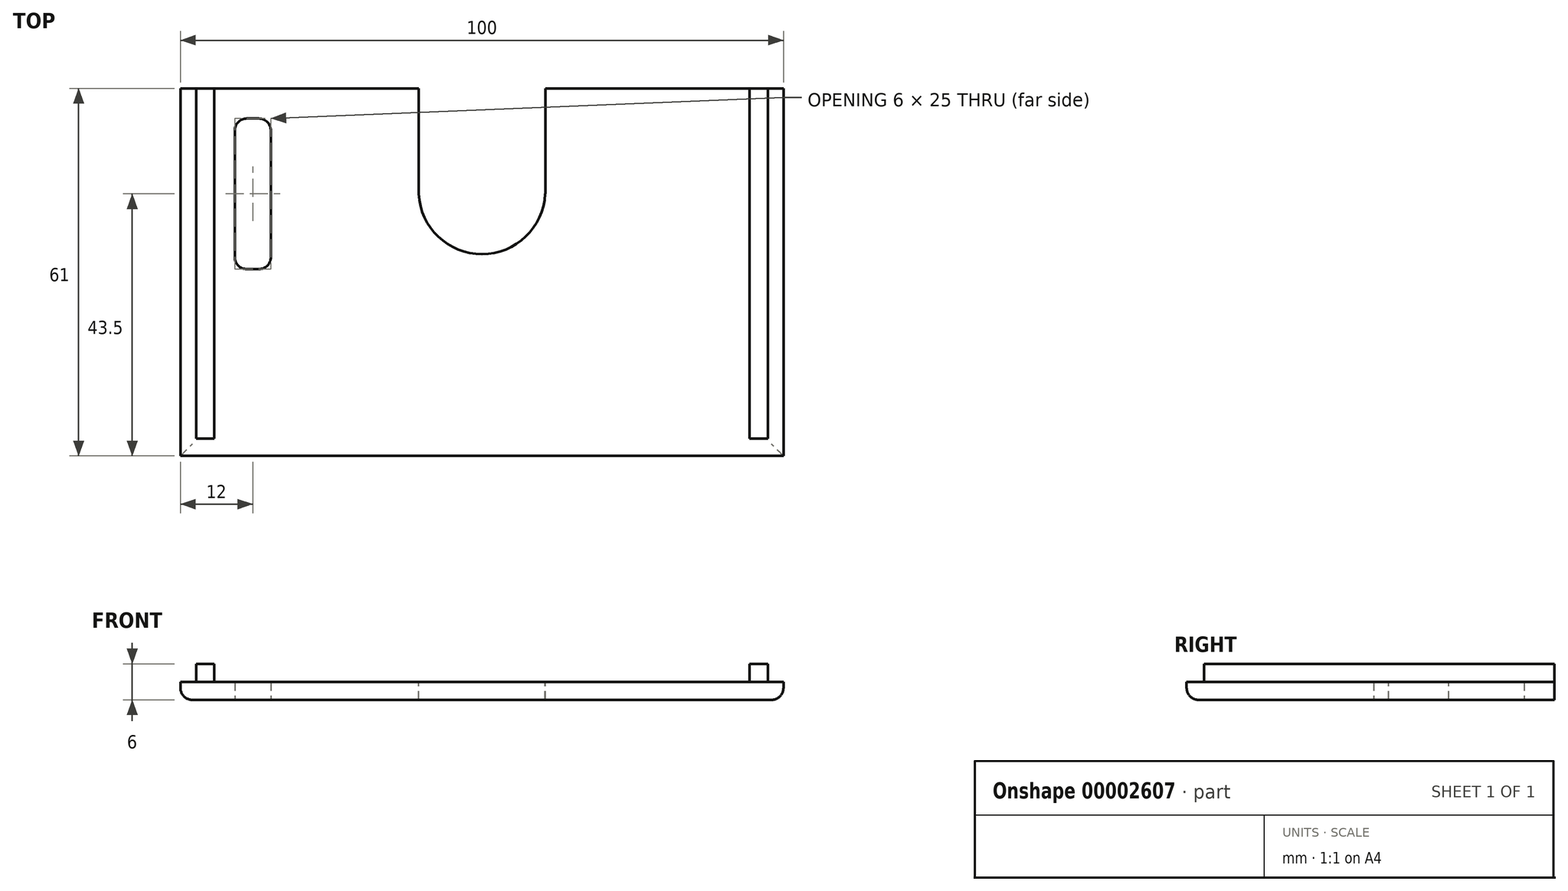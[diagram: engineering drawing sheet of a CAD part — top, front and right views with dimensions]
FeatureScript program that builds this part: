
annotation { "Feature Type Name" : "Feature", "Feature Type Description" : "" }
export const myFeature = defineFeature(function(context is Context, id is Id, definition is map)
    precondition{}
    {
        {
            var Q0;
            Q0=qCreatedBy(makeId("Top.planeOp"),FACE);
            var sketch = newSketch(context, id + "F0", { "sketchPlane" : qUnion([Q0])});
            skLineSegment(sketch, "E0.rect.bottom", {"start": v(-50, 30.5) * mm, "end": v(50, 30.5) * mm});
            skLineSegment(sketch, "E0.rect.top", {"start": v(-50, -30.5) * mm, "end": v(50, -30.5) * mm});
            skLineSegment(sketch, "E0.rect.left", {"start": v(-50, 30.5) * mm, "end": v(-50, -30.5) * mm});
            skLineSegment(sketch, "E0.rect.right", {"start": v(50, 30.5) * mm, "end": v(50, -30.5) * mm});
            skPoint(sketch, "E0.rect.middle", {"position": v(0, 0) * mm});
            skSolve(sketch);
        }
        {
            var Q0;
            Q0=makeQuery(id+"F0.imprint","IMPRINT",FACE,{"disambiguationData":[TD([[makeQuery(id+"F0.imprint","IMPRINT",EDGE,{"derivedFrom":sQuery(id+"F0.wireOp",EDGE,"E0.rect.bottom")}),-1.0]])]});
            extrude(context, id + "F1", {"entities" : qUnion([Q0]), "depth" : 3 * mm});
        }
        {
            var Q0;
            Q0=makeQuery(id+"F1.opExtrude","CAP_FACE",FACE,{"disambiguationData":[OSD([sQuery(id+"F0.wireOp",EDGE,"E0.rect.bottom"),sQuery(id+"F0.wireOp",EDGE,"E0.rect.top"),sQuery(id+"F0.wireOp",EDGE,"E0.rect.left"),sQuery(id+"F0.wireOp",EDGE,"E0.rect.right")])],"isStart":false});
            var sketch = newSketch(context, id + "F2", { "sketchPlane" : qUnion([Q0])});
            skLineSegment(sketch, "E1", {"start": v(0, 30.5) * mm, "end": v(0, 13.5) * mm, "construction": true});
            skCircle(sketch, "E2", {"center": v(0, 13.5) * mm, "radius": 10.5 * mm});
            skLineSegment(sketch, "E3", {"start": v(0, 30.5) * mm, "end": v(0, 22) * mm, "construction": true});
            skLineSegment(sketch, "E4.rect.bottom", {"start": v(-10.5, 31) * mm, "end": v(10.5, 31) * mm});
            skLineSegment(sketch, "E4.rect.top", {"start": v(-10.5, 13) * mm, "end": v(10.5, 13) * mm});
            skLineSegment(sketch, "E4.rect.left", {"start": v(-10.5, 31) * mm, "end": v(-10.5, 13) * mm});
            skLineSegment(sketch, "E4.rect.right", {"start": v(10.5, 31) * mm, "end": v(10.5, 13) * mm});
            skPoint(sketch, "E4.rect.middle", {"position": v(0, 22) * mm});
            skSolve(sketch);
        }
        {
            var Q0;
            {var subQ0=sQuery(id+"F2.wireOp",EDGE,"E4.rect.left");var subQ1=sQuery(id+"F2.wireOp",EDGE,"E2");var subQ2=makeQuery(id+"F2.imprint","INTERSECT",VERTEX,{"derivedFrom":[subQ1,subQ0]});var subQ3=sQuery(id+"F2.wireOp",EDGE,"E4.rect.top");var subQ5=makeQuery(id+"F2.imprint","INTERSECT",VERTEX,{"disambiguationData":[OD(0.0)],"derivedFrom":[subQ1,subQ3]});var subQ6=makeQuery(id+"F2.imprint","IMPRINT",EDGE,{"disambiguationData":[TD([[subQ2,-1.0]])],"derivedFrom":subQ1});var subQ9=sQuery(id+"F2.wireOp",EDGE,"E4.rect.right");var subQ10=makeQuery(id+"F2.imprint","INTERSECT",VERTEX,{"derivedFrom":[subQ1,subQ9]});var subQ12=makeQuery(id+"F2.imprint","IMPRINT",EDGE,{"disambiguationData":[TD([[subQ10,1.0]])],"derivedFrom":subQ1});var subQ13=makeQuery(id+"F2.imprint","IMPRINT",EDGE,{"disambiguationData":[TD([[subQ2,1.0]])],"derivedFrom":subQ1});var subQ18=sQuery(id+"F2.wireOp",EDGE,"E4.rect.bottom");Q0=qUnion([makeQuery(id+"F2.imprint","IMPRINT",FACE,{"disambiguationData":[TD([[subQ6,-1.0]])]}),makeQuery(id+"F2.imprint","IMPRINT",FACE,{"disambiguationData":[TD([[makeQuery(id+"F2.imprint","IMPRINT",EDGE,{"disambiguationData":[TD([[subQ5,-1.0]])],"derivedFrom":subQ1}),1.0]])]}),makeQuery(id+"F2.imprint","IMPRINT",FACE,{"disambiguationData":[TD([[subQ12,-1.0]])]}),makeQuery(id+"F2.imprint","IMPRINT",FACE,{"disambiguationData":[TD([[subQ13,1.0]])]}),makeQuery(id+"F2.imprint","IMPRINT",FACE,{"disambiguationData":[TD([[makeQuery(id+"F2.imprint","IMPRINT",EDGE,{"derivedFrom":subQ18}),-1.0]])]}),makeQuery(id+"F2.imprint","IMPRINT",FACE,{"disambiguationData":[TD([[subQ13,-1.0]])]})]);}
            extrude(context, id + "F3", {"entities" : qUnion([Q0]), "operationType" : NewBodyOperationType.REMOVE, "oppositeDirection" : true, "depth" : 25 * mm});
        }
        {
            var Q0;
            Q0=makeQuery(id+"F1.opExtrude","CAP_FACE",FACE,{"disambiguationData":[OSD([sQuery(id+"F0.wireOp",EDGE,"E0.rect.bottom"),sQuery(id+"F0.wireOp",EDGE,"E0.rect.top"),sQuery(id+"F0.wireOp",EDGE,"E0.rect.left"),sQuery(id+"F0.wireOp",EDGE,"E0.rect.right")])],"isStart":false});
            var sketch = newSketch(context, id + "F4", { "sketchPlane" : qUnion([Q0])});
            skLineSegment(sketch, "E5", {"start": v(-50, -30.5) * mm, "end": v(-44.4, -30.5) * mm, "construction": true});
            skLineSegment(sketch, "E6", {"start": v(-44.4, -30.5) * mm, "end": v(-44.4, -27.6) * mm, "construction": true});
            skLineSegment(sketch, "E7", {"start": v(-50, 30.5) * mm, "end": v(-47.4, 30.5) * mm, "construction": true});
            skLineSegment(sketch, "E8.bottom", {"start": v(-47.4, 30.5) * mm, "end": v(-44.4, 30.5) * mm});
            skLineSegment(sketch, "E8.top", {"start": v(-47.4, -27.6) * mm, "end": v(-44.4, -27.6) * mm});
            skLineSegment(sketch, "E8.left", {"start": v(-47.4, 30.5) * mm, "end": v(-47.4, -27.6) * mm});
            skLineSegment(sketch, "E8.right", {"start": v(-44.4, 30.5) * mm, "end": v(-44.4, -27.6) * mm});
            skLineSegment(sketch, "E9", {"start": v(50, -30.5) * mm, "end": v(44.4, -30.5) * mm, "construction": true});
            skLineSegment(sketch, "E10", {"start": v(44.4, -30.5) * mm, "end": v(44.4, -27.6) * mm, "construction": true});
            skLineSegment(sketch, "E11", {"start": v(50, 30.5) * mm, "end": v(47.4, 30.5) * mm, "construction": true});
            skLineSegment(sketch, "E12.bottom", {"start": v(47.4, 30.5) * mm, "end": v(44.4, 30.5) * mm});
            skLineSegment(sketch, "E12.top", {"start": v(47.4, -27.6) * mm, "end": v(44.4, -27.6) * mm});
            skLineSegment(sketch, "E12.left", {"start": v(47.4, 30.5) * mm, "end": v(47.4, -27.6) * mm});
            skLineSegment(sketch, "E12.right", {"start": v(44.4, 30.5) * mm, "end": v(44.4, -27.6) * mm});
            skSolve(sketch);
        }
        {
            var Q0;
            {Q0=qUnion([makeQuery(id+"F4.imprint","IMPRINT",FACE,{"disambiguationData":[TD([[makeQuery(id+"F4.imprint","IMPRINT",EDGE,{"derivedFrom":sQuery(id+"F4.wireOp",EDGE,"E8.bottom")}),-1.0]])]}),makeQuery(id+"F4.imprint","IMPRINT",FACE,{"disambiguationData":[TD([[makeQuery(id+"F4.imprint","IMPRINT",EDGE,{"derivedFrom":sQuery(id+"F4.wireOp",EDGE,"E12.bottom")}),-1.0]])]})]);}
            extrude(context, id + "F5", {"entities" : qUnion([Q0]), "operationType" : NewBodyOperationType.ADD, "depth" : 3 * mm});
        }
        {
            var Q0;
            Q0=makeQuery(id+"F1.opExtrude","CAP_EDGE",EDGE,{"disambiguationData":[OSD([sQuery(id+"F0.wireOp",EDGE,"E0.rect.right")])],"isStart":true});
            var Q1;
            Q1=makeQuery(id+"F1.opExtrude","CAP_EDGE",EDGE,{"disambiguationData":[OSD([sQuery(id+"F0.wireOp",EDGE,"E0.rect.left")])],"isStart":true});
            var Q2;
            Q2=makeQuery(id+"F1.opExtrude","CAP_EDGE",EDGE,{"disambiguationData":[OSD([sQuery(id+"F0.wireOp",EDGE,"E0.rect.top")])],"isStart":true});
            fillet(context, id + "F6", {"entities" : qUnion([Q0, Q1, Q2]), "radius" : 2 * mm, "tangentPropagation" : true, "allowEdgeOverflow" : false});
        }
        {
            var Q0;
            Q0=makeQuery(id+"F1.opExtrude","CAP_FACE",FACE,{"disambiguationData":[OSD([sQuery(id+"F0.wireOp",EDGE,"E0.rect.bottom"),sQuery(id+"F0.wireOp",EDGE,"E0.rect.top"),sQuery(id+"F0.wireOp",EDGE,"E0.rect.left"),sQuery(id+"F0.wireOp",EDGE,"E0.rect.right")])],"isStart":true});
            var sketch = newSketch(context, id + "F7", { "sketchPlane" : qUnion([Q0])});
            skLineSegment(sketch, "E13", {"start": v(-48, -30.5) * mm, "end": v(-38, -30.5) * mm, "construction": true});
            skLineSegment(sketch, "E14", {"start": v(-38, -30.5) * mm, "end": v(-38, -13) * mm, "construction": true});
            skLineSegment(sketch, "E15.rect.bottom", {"start": v(-35, -25.5) * mm, "end": v(-41, -25.5) * mm});
            skLineSegment(sketch, "E15.rect.top", {"start": v(-35, -0.5) * mm, "end": v(-41, -0.5) * mm});
            skLineSegment(sketch, "E15.rect.left", {"start": v(-35, -25.5) * mm, "end": v(-35, -0.5) * mm});
            skLineSegment(sketch, "E15.rect.right", {"start": v(-41, -25.5) * mm, "end": v(-41, -0.5) * mm});
            skPoint(sketch, "E15.rect.middle", {"position": v(-38, -13) * mm});
            skSolve(sketch);
        }
        {
            var Q0;
            Q0=makeQuery(id+"F7.imprint","IMPRINT",FACE,{"disambiguationData":[TD([[makeQuery(id+"F7.imprint","IMPRINT",EDGE,{"derivedFrom":sQuery(id+"F7.wireOp",EDGE,"E15.rect.bottom")}),-1.0]])]});
            extrude(context, id + "F8", {"entities" : qUnion([Q0]), "operationType" : NewBodyOperationType.REMOVE, "oppositeDirection" : true, "depth" : 25 * mm});
        }
        {
            var Q0;
            Q0=makeQuery(id+"F8.boolean.opBoolean","COPY",EDGE,{"derivedFrom":makeQuery(id+"F8.opExtrude","SWEPT_EDGE",EDGE,{"disambiguationData":[OSD([sQuery(id+"F7.wireOp",EDGE,"E15.rect.bottom"),sQuery(id+"F7.wireOp",EDGE,"E15.rect.left")])]})});
            var Q1;
            Q1=makeQuery(id+"F8.boolean.opBoolean","COPY",EDGE,{"derivedFrom":makeQuery(id+"F8.opExtrude","SWEPT_EDGE",EDGE,{"disambiguationData":[OSD([sQuery(id+"F7.wireOp",EDGE,"E15.rect.bottom"),sQuery(id+"F7.wireOp",EDGE,"E15.rect.right")])]})});
            var Q2;
            Q2=makeQuery(id+"F8.boolean.opBoolean","COPY",EDGE,{"derivedFrom":makeQuery(id+"F8.opExtrude","SWEPT_EDGE",EDGE,{"disambiguationData":[OSD([sQuery(id+"F7.wireOp",EDGE,"E15.rect.top"),sQuery(id+"F7.wireOp",EDGE,"E15.rect.right")])]})});
            var Q3;
            Q3=makeQuery(id+"F8.boolean.opBoolean","COPY",EDGE,{"derivedFrom":makeQuery(id+"F8.opExtrude","SWEPT_EDGE",EDGE,{"disambiguationData":[OSD([sQuery(id+"F7.wireOp",EDGE,"E15.rect.top"),sQuery(id+"F7.wireOp",EDGE,"E15.rect.left")])]})});
            fillet(context, id + "F9", {"entities" : qUnion([Q0, Q1, Q2, Q3]), "radius" : 2 * mm, "tangentPropagation" : true, "allowEdgeOverflow" : false});
        }
    });
